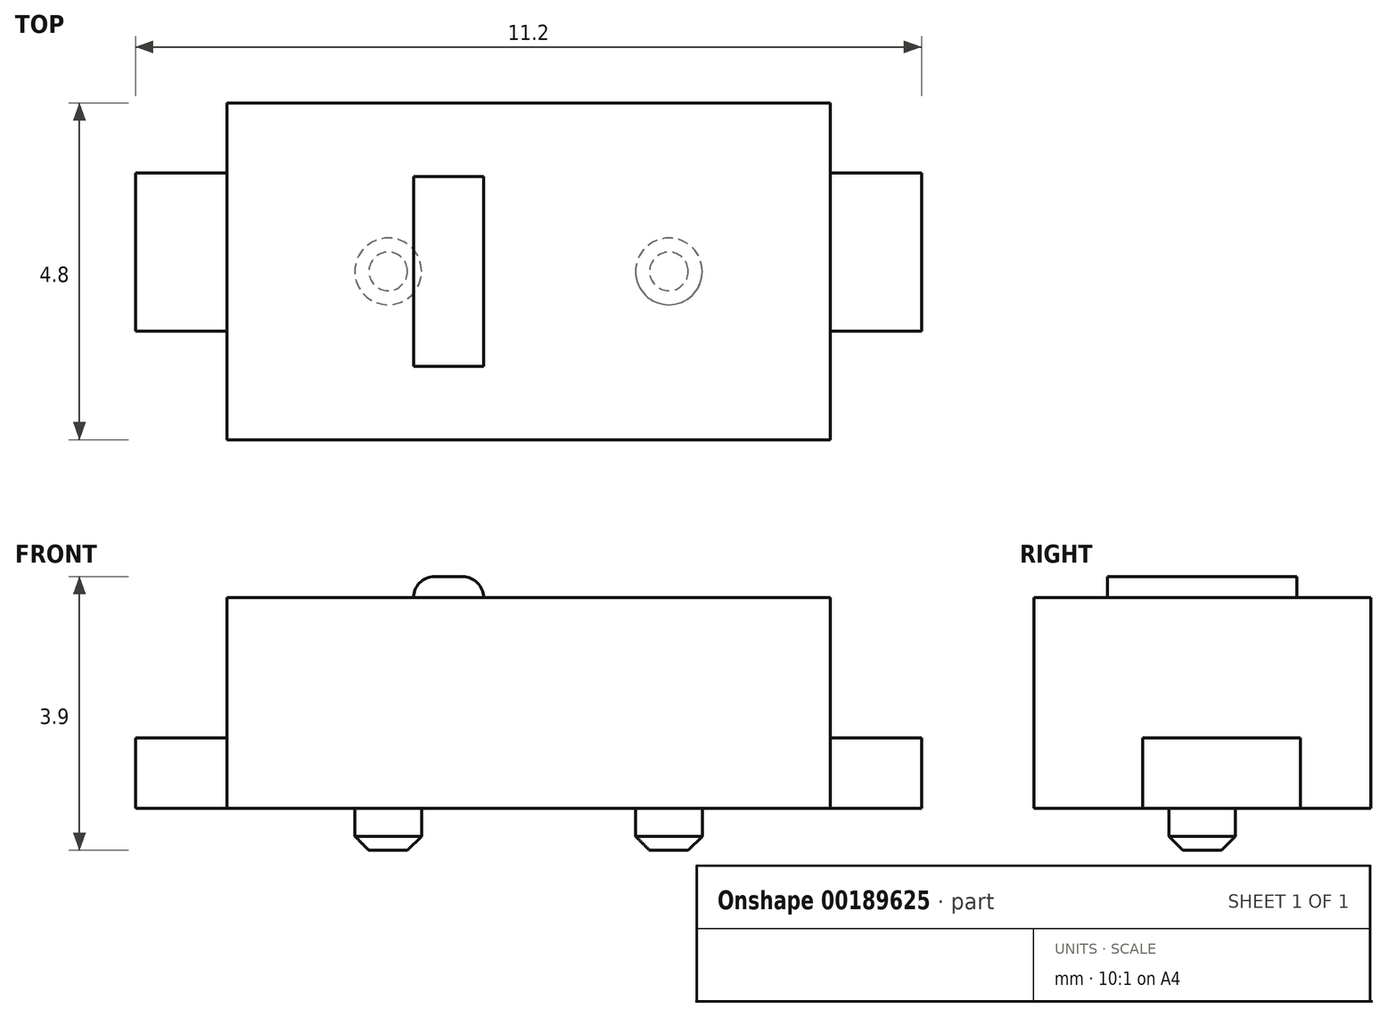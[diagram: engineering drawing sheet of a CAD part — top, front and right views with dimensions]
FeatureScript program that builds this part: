
annotation { "Feature Type Name" : "Feature", "Feature Type Description" : "" }
export const myFeature = defineFeature(function(context is Context, id is Id, definition is map)
    precondition{}
    {
        {
            var Q0;
            Q0=qCreatedBy(makeId("Top.planeOp"),FACE);
            var sketch = newSketch(context, id + "F0", { "sketchPlane" : qUnion([Q0])});
            skLineSegment(sketch, "E0.bottom", {"start": v(4.3, 2.4) * mm, "end": v(-4.3, 2.4) * mm});
            skLineSegment(sketch, "E0.top", {"start": v(4.3, -2.4) * mm, "end": v(-4.3, -2.4) * mm});
            skLineSegment(sketch, "E0.left", {"start": v(4.3, 2.4) * mm, "end": v(4.3, -2.4) * mm});
            skLineSegment(sketch, "E0.right", {"start": v(-4.3, 2.4) * mm, "end": v(-4.3, -2.4) * mm});
            skPoint(sketch, "E0.middle", {"position": v(0, 0) * mm});
            skSolve(sketch);
        }
        {
            var Q0;
            Q0 = qSketchRegion(id + "F0", true);
            extrude(context, id + "F1", {"entities" : qUnion([Q0]), "depth" : 3 * mm});
        }
        {
            var Q0;
            Q0=makeQuery(id+"F1.opExtrude","CAP_FACE",FACE,{"disambiguationData":[OSD([sQuery(id+"F0.wireOp",EDGE,"E0.bottom"),sQuery(id+"F0.wireOp",EDGE,"E0.top"),sQuery(id+"F0.wireOp",EDGE,"E0.left"),sQuery(id+"F0.wireOp",EDGE,"E0.right")])],"isStart":true});
            var sketch = newSketch(context, id + "F2", { "sketchPlane" : qUnion([Q0])});
            skCircle(sketch, "E1", {"center": v(-2, 0) * mm, "radius": 0.47 * mm});
            skCircle(sketch, "E2", {"center": v(2, 0) * mm, "radius": 0.47 * mm});
            skSolve(sketch);
        }
        {
            var Q0;
            Q0 = qSketchRegion(id + "F2", true);
            extrude(context, id + "F3", {"entities" : qUnion([Q0]), "operationType" : NewBodyOperationType.ADD, "depth" : 0.6 * mm});
        }
        {
            var Q0;
            Q0=makeQuery(id+"F3.opExtrude","CAP_EDGE",EDGE,{"disambiguationData":[OSD([sQuery(id+"F2.wireOp",EDGE,"E1")])],"isStart":false});
            var Q1;
            Q1=makeQuery(id+"F3.opExtrude","CAP_EDGE",EDGE,{"disambiguationData":[OSD([sQuery(id+"F2.wireOp",EDGE,"E2")])],"isStart":false});
            chamfer(context, id + "F4", {"entities" : qUnion([Q0, Q1]), "width" : 0.2 * mm, "tangentPropagation" : true});
        }
        {
            var Q0;
            Q0=qCreatedBy(makeId("Top.planeOp"),FACE);
            var sketch = newSketch(context, id + "F5", { "sketchPlane" : qUnion([Q0])});
            skLineSegment(sketch, "E3.bottom", {"start": v(-5.6, 1.4) * mm, "end": v(-4.3, 1.4) * mm});
            skLineSegment(sketch, "E3.top", {"start": v(-5.6, -0.85) * mm, "end": v(-4.3, -0.85) * mm});
            skLineSegment(sketch, "E3.left", {"start": v(-5.6, 1.4) * mm, "end": v(-5.6, -0.85) * mm});
            skLineSegment(sketch, "E3.right", {"start": v(-4.3, 1.4) * mm, "end": v(-4.3, -0.85) * mm});
            skLineSegment(sketch, "E4.bottom", {"start": v(5.6, 1.4) * mm, "end": v(4.3, 1.4) * mm});
            skLineSegment(sketch, "E4.top", {"start": v(5.6, -0.85) * mm, "end": v(4.3, -0.85) * mm});
            skLineSegment(sketch, "E4.left", {"start": v(5.6, 1.4) * mm, "end": v(5.6, -0.85) * mm});
            skLineSegment(sketch, "E4.right", {"start": v(4.3, 1.4) * mm, "end": v(4.3, -0.85) * mm});
            skPoint(sketch, "E5", {"position": v(-4.3, 0) * mm});
            skPoint(sketch, "E6", {"position": v(4.3, 0) * mm});
            skSolve(sketch);
        }
        {
            var Q0;
            Q0 = qSketchRegion(id + "F5", true);
            extrude(context, id + "F6", {"entities" : qUnion([Q0]), "operationType" : NewBodyOperationType.ADD, "depth" : 1 * mm});
        }
        {
            var Q0;
            Q0=makeQuery(id+"F1.opExtrude","CAP_FACE",FACE,{"disambiguationData":[OSD([sQuery(id+"F0.wireOp",EDGE,"E0.bottom"),sQuery(id+"F0.wireOp",EDGE,"E0.top"),sQuery(id+"F0.wireOp",EDGE,"E0.left"),sQuery(id+"F0.wireOp",EDGE,"E0.right")])],"isStart":false});
            var sketch = newSketch(context, id + "F7", { "sketchPlane" : qUnion([Q0])});
            skLineSegment(sketch, "E7.bottom", {"start": v(-0.64, 1.35) * mm, "end": v(-1.64, 1.35) * mm});
            skLineSegment(sketch, "E7.top", {"start": v(-0.64, -1.35) * mm, "end": v(-1.64, -1.35) * mm});
            skLineSegment(sketch, "E7.left", {"start": v(-0.64, 1.35) * mm, "end": v(-0.64, -1.35) * mm});
            skLineSegment(sketch, "E7.right", {"start": v(-1.64, 1.35) * mm, "end": v(-1.64, -1.35) * mm});
            skPoint(sketch, "E7.middle", {"position": v(-1.14, 0) * mm});
            skLineSegment(sketch, "E8", {"start": v(-1.14, 0) * mm, "end": v(0, 0) * mm, "construction": true});
            skSolve(sketch);
        }
        {
            var Q0;
            Q0 = qSketchRegion(id + "F7", true);
            var Q1;
            Q1 = qConstructionFilter(qBodyType(qCreatedBy(id + "F7" ,EDGE), BodyType.WIRE), ConstructionObject.NO);
            extrude(context, id + "F8", {"entities" : qUnion([Q0]), "operationType" : NewBodyOperationType.ADD, "surfaceEntities" : qUnion([Q1]), "depth" : 0.3 * mm});
        }
        {
            var Q0;
            Q0=makeQuery(id+"F8.opExtrude","CAP_EDGE",EDGE,{"disambiguationData":[OSD([sQuery(id+"F7.wireOp",EDGE,"E7.right")])],"isStart":false});
            var Q1;
            Q1=makeQuery(id+"F8.opExtrude","CAP_EDGE",EDGE,{"disambiguationData":[OSD([sQuery(id+"F7.wireOp",EDGE,"E7.left")])],"isStart":false});
            fillet(context, id + "F9", {"entities" : qUnion([Q0, Q1]), "radius" : 0.3 * mm, "tangentPropagation" : true, "allowEdgeOverflow" : false});
        }
        {
            var Q0;
            Q0=makeQuery(id+"F1.opExtrude","SWEPT_BODY",BODY,{"disambiguationData":[OSD([sQuery(id+"F0.wireOp",EDGE,"E0.bottom"),sQuery(id+"F0.wireOp",EDGE,"E0.top"),sQuery(id+"F0.wireOp",EDGE,"E0.left"),sQuery(id+"F0.wireOp",EDGE,"E0.right")])]});
            var Q1;
            Q1=sQuery(id+"F7.wireOp",EDGE,"E8");
            transform(context, id + "F10", {"entities" : qUnion([Q0]), "transformType" : TransformType.TRANSLATION_ENTITY, "oppositeDirectionEntity" : false, "transformLine" : qUnion([Q1]), "makeCopy" : false});
        }
    });
